# Revit family: 123Electronics_Commercial-Loudspeakers_Biamp_Dispersion-Sphere-Loudspeaker_SPH20
name_source: partatom
category: Communication Devices
units: mm (PartAtom-declared; Revit-internal decimal feet)

## family parameters
Cut with Voids When Loaded = No
Host = Face
Maintain Annotation Orientation = No
OmniClass Number = 23.85.10.11.14.14.14
OmniClass Title = Loudspeakers
Part Type = Normal
Room Calculation Point = No
Round Connector Dimension = Use Diameter
Shared = No

## types (1)
- SPH20
    100V transformer power taps in watts = 20 - 10 -5
    Default Elevation = 0 "
    Description = SPH20 360° Dispersion Sphere Loudspeaker
    Diameter = 10.04 "
    Frequency response in Hz = 80-18k
    Housing Material = Biamp - Plastic - White
    Impedance (ohms) = 8
    Loudspeaker system = Dual cone
    Low impedance RMS power in watts = 20
    Low impedance dynamic power in watts = 30
    Manufacturer = Biamp
    Max SPL 1m in dB = 111
    Model = SPH20
    Mounting system = Ceiling socket
    Product Documentation Link = https://downloads.biamp.com
    Product Page URL = https://www.biamp.com
    Product data url = https://bimobject.com
    SPL 1W/1m in dB = 95
    URL = https://www.biamp.com
    Vertical dispersion angle 1000 Hz = 110°
    Weight = 4.85 lbf
    Woofer cone material = Paper
    Woofer size in inch = 8

## geometry (parser evidence)
native form markers: Sweep x2
no freeform markers — native parametric forms only
